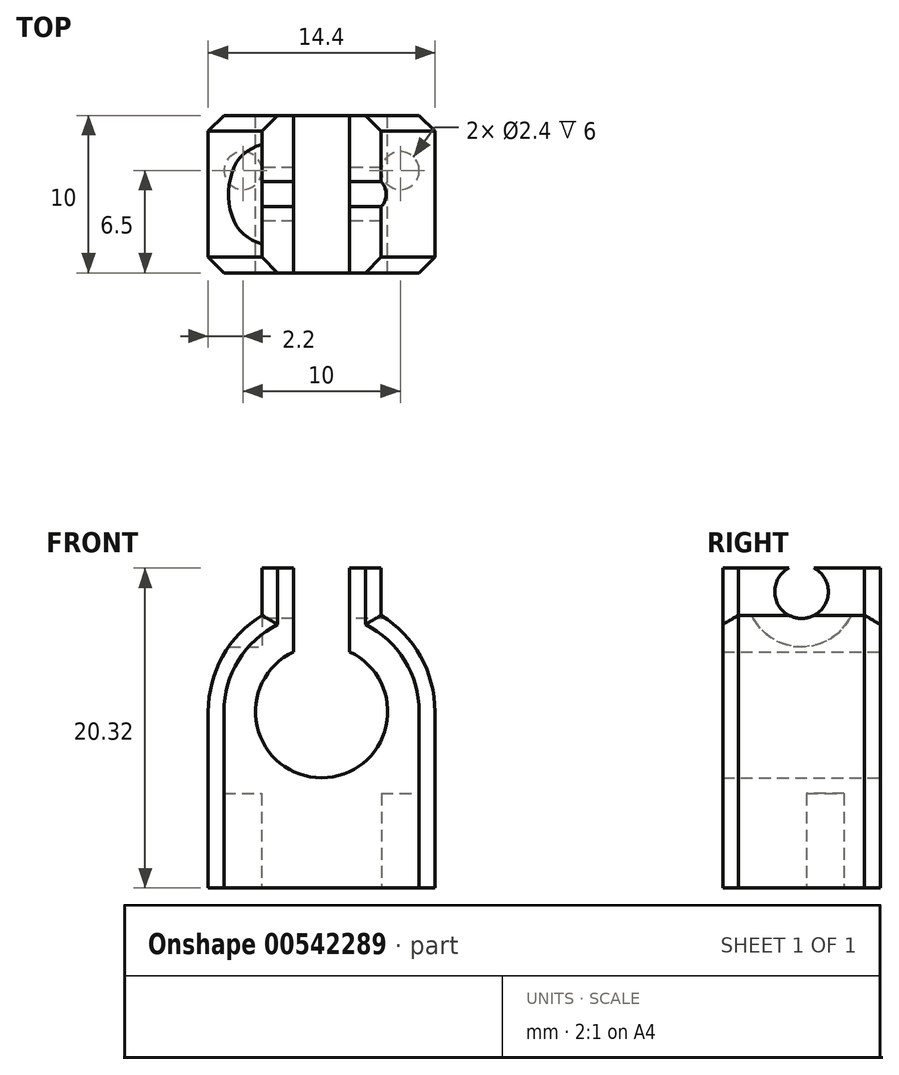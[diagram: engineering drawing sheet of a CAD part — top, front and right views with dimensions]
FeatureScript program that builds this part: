
annotation { "Feature Type Name" : "Feature", "Feature Type Description" : "" }
export const myFeature = defineFeature(function(context is Context, id is Id, definition is map)
    precondition{}
    {
        {
            var Q0;
            Q0=qCreatedBy(makeId("Front.planeOp"),FACE);
            var sketch = newSketch(context, id + "F0", { "sketchPlane" : qUnion([Q0])});
            skArc(sketch, "E0", {"start": v(-1.79, 3.8) * mm, "mid": v(0, -4.2) * mm, "end": v(1.79, 3.8) * mm});
            skArc(sketch, "E1", {"start": v(-3.79, 6.12) * mm, "mid": v(-6.29, 3.5) * mm, "end": v(-7.2, 0) * mm});
            skLineSegment(sketch, "E2", {"start": v(0, 0) * mm, "end": v(-1.79, 0) * mm, "construction": true});
            skLineSegment(sketch, "E3", {"start": v(0, 0) * mm, "end": v(1.79, 0) * mm, "construction": true});
            skLineSegment(sketch, "E4", {"start": v(-1.79, 3.8) * mm, "end": v(-1.79, 6.97) * mm});
            skLineSegment(sketch, "E5", {"start": v(1.79, 3.8) * mm, "end": v(1.79, 6.97) * mm});
            skLineSegment(sketch, "E6", {"start": v(-1.79, 6.97) * mm, "end": v(-1.79, 9.12) * mm});
            skLineSegment(sketch, "E7", {"start": v(-1.79, 9.12) * mm, "end": v(-3.79, 9.12) * mm});
            skLineSegment(sketch, "E8", {"start": v(-3.79, 9.12) * mm, "end": v(-3.79, 6.12) * mm});
            skLineSegment(sketch, "E9", {"start": v(0, 0) * mm, "end": v(0, 11.52) * mm, "construction": true});
            skLineSegment(sketch, "E10.MirrorCS", {"start": v(1.79, 9.12) * mm, "end": v(3.79, 9.12) * mm});
            skLineSegment(sketch, "E11.MirrorCS", {"start": v(3.79, 9.12) * mm, "end": v(3.79, 6.12) * mm});
            skLineSegment(sketch, "E12.MirrorCS", {"start": v(1.79, 6.97) * mm, "end": v(1.79, 9.12) * mm});
            skLineSegment(sketch, "E13", {"start": v(-7.2, 0) * mm, "end": v(-7.2, -11.2) * mm});
            skLineSegment(sketch, "E14", {"start": v(7.2, 0) * mm, "end": v(7.2, -11.2) * mm});
            skLineSegment(sketch, "E15", {"start": v(7.2, -11.2) * mm, "end": v(-7.2, -11.2) * mm});
            skLineSegment(sketch, "E16", {"start": v(0, -7.2) * mm, "end": v(0, -11.2) * mm, "construction": true});
            skArc(sketch, "E17.trimOffspring", {"start": v(7.2, 0) * mm, "mid": v(6.29, 3.5) * mm, "end": v(3.79, 6.12) * mm});
            skSolve(sketch);
        }
        {
            var Q0;
            Q0=makeQuery(id+"F0.imprint","IMPRINT",FACE,{"disambiguationData":[TD([[makeQuery(id+"F0.imprint","IMPRINT",EDGE,{"derivedFrom":sQuery(id+"F0.wireOp",EDGE,"E0")}),-1.0]])]});
            extrude(context, id + "F1", {"entities" : qUnion([Q0]), "depth" : 10 * mm, "offsetDistance" : 25 * mm});
        }
        {
            var Q0;
            Q0=makeQuery(id+"F1.opExtrude","SWEPT_FACE",FACE,{"disambiguationData":[OSD([sQuery(id+"F0.wireOp",EDGE,"E8")])]});
            var sketch = newSketch(context, id + "F2", { "sketchPlane" : qUnion([Q0])});
            skLineSegment(sketch, "E18", {"start": v(0, 7.62) * mm, "end": v(10, 7.62) * mm, "construction": true});
            skLineSegment(sketch, "E19", {"start": v(5, 9.12) * mm, "end": v(5, 6.12) * mm, "construction": true});
            skCircle(sketch, "E20", {"center": v(5, 7.62) * mm, "radius": 1.7 * mm});
            skCircle(sketch, "E21", {"center": v(5, 7.62) * mm, "radius": 3.5 * mm});
            skSolve(sketch);
        }
        {
            var Q0;
            {var subQ0=sQuery(id+"F2.wireOp",EDGE,"E20");var subQ1=makeQuery(id+"F1.opExtrude","SWEPT_EDGE",EDGE,{"disambiguationData":[OSD([sQuery(id+"F0.wireOp",EDGE,"E1"),sQuery(id+"F0.wireOp",EDGE,"E8")])]});var subQ2=makeQuery(id+"F2.imprint","INTERSECT",VERTEX,{"disambiguationData":[OD(0.0)],"derivedFrom":[subQ1,subQ0]});Q0=makeQuery(id+"F2.imprint","IMPRINT",FACE,{"disambiguationData":[TD([[makeQuery(id+"F2.imprint","IMPRINT",EDGE,{"disambiguationData":[TD([[subQ2,-1.0]])],"derivedFrom":subQ0}),-1.0]])]});}
            var Q1;
            {var subQ0=sQuery(id+"F2.wireOp",EDGE,"E20");var subQ1=sQuery(id+"F0.wireOp",EDGE,"E8");var subQ2=makeQuery(id+"F1.opExtrude","SWEPT_EDGE",EDGE,{"disambiguationData":[OSD([sQuery(id+"F0.wireOp",EDGE,"E7"),subQ1])]});var subQ3=makeQuery(id+"F2.imprint","INTERSECT",VERTEX,{"disambiguationData":[OD(0.0)],"derivedFrom":[subQ2,subQ0]});Q1=makeQuery(id+"F2.imprint","IMPRINT",FACE,{"disambiguationData":[TD([[makeQuery(id+"F2.imprint","IMPRINT",EDGE,{"disambiguationData":[TD([[subQ3,-1.0]])],"derivedFrom":subQ0}),-1.0]])]});}
            var Q2;
            {var subQ0=sQuery(id+"F2.wireOp",EDGE,"E20");var subQ1=makeQuery(id+"F1.opExtrude","SWEPT_EDGE",EDGE,{"disambiguationData":[OSD([sQuery(id+"F0.wireOp",EDGE,"E7"),sQuery(id+"F0.wireOp",EDGE,"E8")])]});var subQ2=makeQuery(id+"F2.imprint","INTERSECT",VERTEX,{"disambiguationData":[OD(0.0)],"derivedFrom":[subQ1,subQ0]});Q2=makeQuery(id+"F2.imprint","IMPRINT",FACE,{"disambiguationData":[TD([[makeQuery(id+"F2.imprint","IMPRINT",EDGE,{"disambiguationData":[TD([[subQ2,1.0]])],"derivedFrom":subQ0}),-1.0]])]});}
            var Q3;
            {var subQ0=sQuery(id+"F2.wireOp",EDGE,"E20");var subQ1=sQuery(id+"F0.wireOp",EDGE,"E8");var subQ2=makeQuery(id+"F1.opExtrude","SWEPT_EDGE",EDGE,{"disambiguationData":[OSD([sQuery(id+"F0.wireOp",EDGE,"E7"),subQ1])]});var subQ3=makeQuery(id+"F2.imprint","INTERSECT",VERTEX,{"disambiguationData":[OD(1.0)],"derivedFrom":[subQ2,subQ0]});Q3=makeQuery(id+"F2.imprint","IMPRINT",FACE,{"disambiguationData":[TD([[makeQuery(id+"F2.imprint","IMPRINT",EDGE,{"disambiguationData":[TD([[subQ3,1.0]])],"derivedFrom":subQ0}),-1.0]])]});}
            extrude(context, id + "F3", {"entities" : qUnion([Q0, Q1, Q2, Q3]), "operationType" : NewBodyOperationType.REMOVE, "depth" : 4 * mm, "offsetDistance" : 25 * mm});
        }
        {
            var Q0;
            {var subQ0=sQuery(id+"F2.wireOp",EDGE,"E20");var subQ1=sQuery(id+"F0.wireOp",EDGE,"E8");var subQ2=makeQuery(id+"F1.opExtrude","SWEPT_EDGE",EDGE,{"disambiguationData":[OSD([sQuery(id+"F0.wireOp",EDGE,"E7"),subQ1])]});var subQ3=makeQuery(id+"F2.imprint","INTERSECT",VERTEX,{"disambiguationData":[OD(0.0)],"derivedFrom":[subQ2,subQ0]});Q0=makeQuery(id+"F2.imprint","IMPRINT",FACE,{"disambiguationData":[TD([[makeQuery(id+"F2.imprint","IMPRINT",EDGE,{"disambiguationData":[TD([[subQ3,-1.0]])],"derivedFrom":subQ0}),1.0]])]});}
            var Q1;
            {var subQ0=sQuery(id+"F2.wireOp",EDGE,"E20");var subQ1=makeQuery(id+"F1.opExtrude","SWEPT_EDGE",EDGE,{"disambiguationData":[OSD([sQuery(id+"F0.wireOp",EDGE,"E7"),sQuery(id+"F0.wireOp",EDGE,"E8")])]});var subQ2=makeQuery(id+"F2.imprint","INTERSECT",VERTEX,{"disambiguationData":[OD(0.0)],"derivedFrom":[subQ1,subQ0]});Q1=makeQuery(id+"F2.imprint","IMPRINT",FACE,{"disambiguationData":[TD([[makeQuery(id+"F2.imprint","IMPRINT",EDGE,{"disambiguationData":[TD([[subQ2,1.0]])],"derivedFrom":subQ0}),1.0]])]});}
            var Q2;
            {var subQ0=sQuery(id+"F2.wireOp",EDGE,"E20");var subQ1=makeQuery(id+"F1.opExtrude","SWEPT_EDGE",EDGE,{"disambiguationData":[OSD([sQuery(id+"F0.wireOp",EDGE,"E1"),sQuery(id+"F0.wireOp",EDGE,"E8")])]});var subQ2=makeQuery(id+"F2.imprint","INTERSECT",VERTEX,{"disambiguationData":[OD(0.0)],"derivedFrom":[subQ1,subQ0]});Q2=makeQuery(id+"F2.imprint","IMPRINT",FACE,{"disambiguationData":[TD([[makeQuery(id+"F2.imprint","IMPRINT",EDGE,{"disambiguationData":[TD([[subQ2,-1.0]])],"derivedFrom":subQ0}),1.0]])]});}
            extrude(context, id + "F4", {"entities" : qUnion([Q0, Q1, Q2]), "operationType" : NewBodyOperationType.REMOVE, "endBound" : BoundingType.SYMMETRIC, "oppositeDirection" : true, "depth" : 40 * mm, "offsetDistance" : 25 * mm});
        }
        {
            var Q0;
            Q0=makeQuery(id+"F1.opExtrude","SWEPT_FACE",FACE,{"disambiguationData":[OSD([sQuery(id+"F0.wireOp",EDGE,"E15")])]});
            var sketch = newSketch(context, id + "F5", { "sketchPlane" : qUnion([Q0])});
            skLineSegment(sketch, "E22", {"start": v(-7.2, 0) * mm, "end": v(-7.2, 3.5) * mm, "construction": true});
            skLineSegment(sketch, "E23", {"start": v(-7.2, 3.5) * mm, "end": v(-5, 3.5) * mm, "construction": true});
            skLineSegment(sketch, "E24", {"start": v(-5, 3.5) * mm, "end": v(5, 3.5) * mm, "construction": true});
            skCircle(sketch, "E25", {"center": v(-5, 3.5) * mm, "radius": 1.2 * mm});
            skCircle(sketch, "E26", {"center": v(5, 3.5) * mm, "radius": 1.2 * mm});
            skSolve(sketch);
        }
        {
            var Q0;
            Q0=makeQuery(id+"F5.imprint","IMPRINT",FACE,{"disambiguationData":[TD([[makeQuery(id+"F5.imprint","IMPRINT",EDGE,{"derivedFrom":sQuery(id+"F5.wireOp",EDGE,"E25")}),1.0]])]});
            var Q1;
            Q1=makeQuery(id+"F5.imprint","IMPRINT",FACE,{"disambiguationData":[TD([[makeQuery(id+"F5.imprint","IMPRINT",EDGE,{"derivedFrom":sQuery(id+"F5.wireOp",EDGE,"E26")}),1.0]])]});
            extrude(context, id + "F6", {"entities" : qUnion([Q0, Q1]), "operationType" : NewBodyOperationType.REMOVE, "oppositeDirection" : true, "depth" : 6 * mm, "offsetDistance" : 25 * mm});
        }
        {
            var Q0;
            Q0=makeQuery(id+"F1.opExtrude","CAP_EDGE",EDGE,{"disambiguationData":[OSD([sQuery(id+"F0.wireOp",EDGE,"E14")])],"isStart":true});
            var Q1;
            Q1=makeQuery(id+"F1.opExtrude","CAP_EDGE",EDGE,{"disambiguationData":[OSD([sQuery(id+"F0.wireOp",EDGE,"E14")])],"isStart":false});
            var Q2;
            Q2=makeQuery(id+"F1.opExtrude","CAP_EDGE",EDGE,{"disambiguationData":[OSD([sQuery(id+"F0.wireOp",EDGE,"E13")])],"isStart":false});
            var Q3;
            Q3=makeQuery(id+"F1.opExtrude","CAP_EDGE",EDGE,{"disambiguationData":[OSD([sQuery(id+"F0.wireOp",EDGE,"E13")])],"isStart":true});
            var Q4;
            Q4=makeQuery(id+"F1.opExtrude","CAP_EDGE",EDGE,{"disambiguationData":[OSD([sQuery(id+"F0.wireOp",EDGE,"E11.MirrorCS")])],"isStart":false});
            var Q5;
            Q5=makeQuery(id+"F1.opExtrude","CAP_EDGE",EDGE,{"disambiguationData":[OSD([sQuery(id+"F0.wireOp",EDGE,"E11.MirrorCS")])],"isStart":true});
            var Q6;
            Q6=makeQuery(id+"F1.opExtrude","CAP_EDGE",EDGE,{"disambiguationData":[OSD([sQuery(id+"F0.wireOp",EDGE,"E8")])],"isStart":false});
            var Q7;
            Q7=makeQuery(id+"F1.opExtrude","CAP_EDGE",EDGE,{"disambiguationData":[OSD([sQuery(id+"F0.wireOp",EDGE,"E8")])],"isStart":true});
            chamfer(context, id + "F7", {"entities" : qUnion([Q0, Q1, Q2, Q3, Q4, Q5, Q6, Q7]), "width" : 1 * mm, "tangentPropagation" : true});
        }
    });
